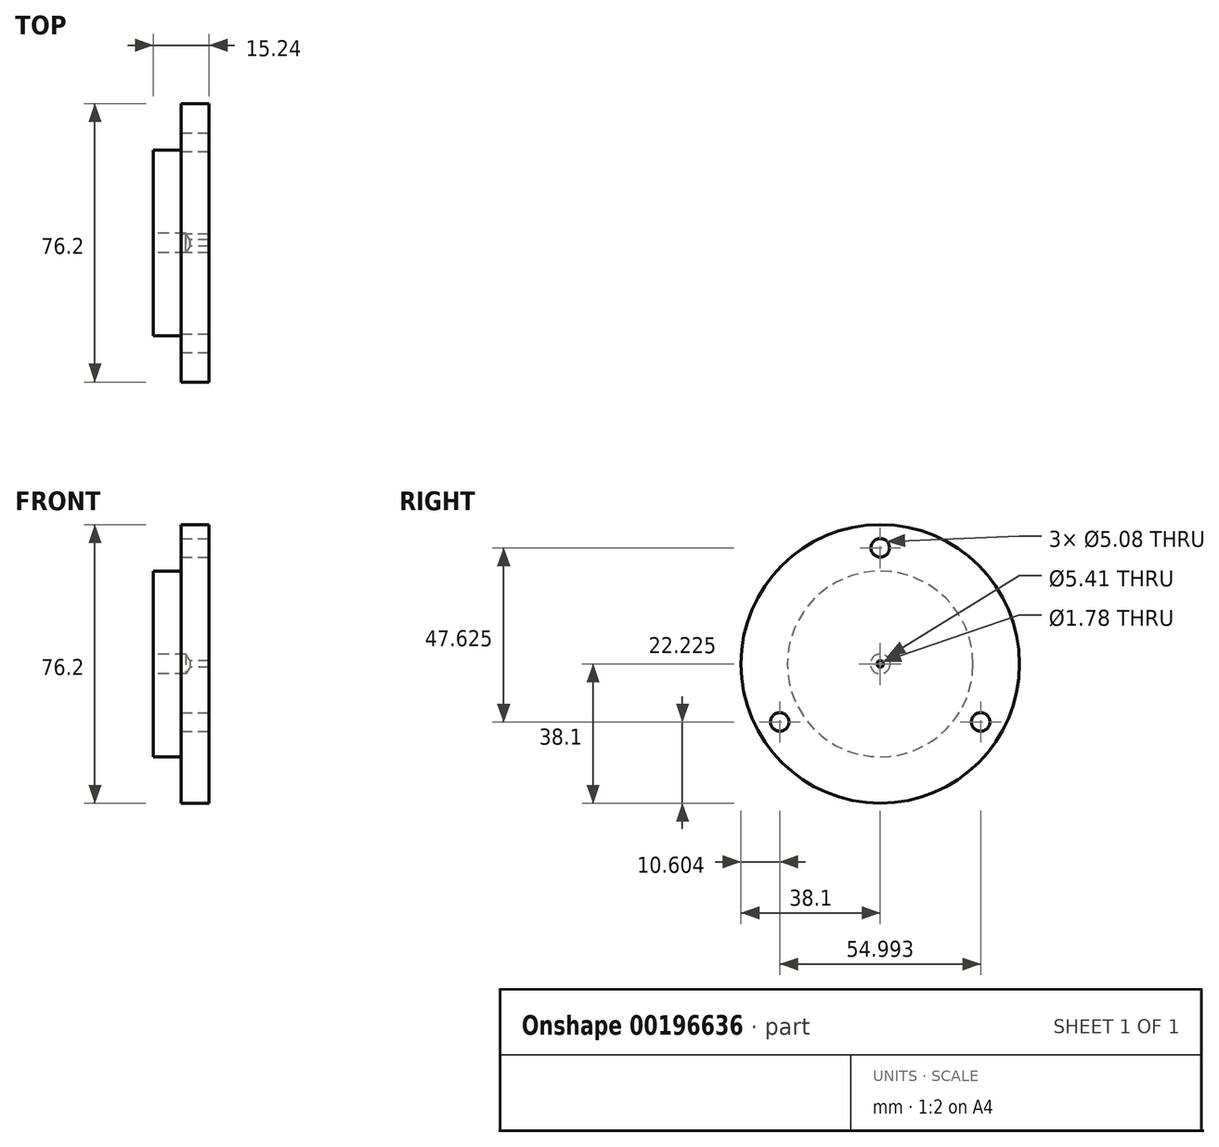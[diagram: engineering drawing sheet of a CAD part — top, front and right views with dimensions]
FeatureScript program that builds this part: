
annotation { "Feature Type Name" : "Feature", "Feature Type Description" : "" }
export const myFeature = defineFeature(function(context is Context, id is Id, definition is map)
    precondition{}
    {
        {
            var Q0;
            Q0=qCreatedBy(makeId("Right.planeOp"),FACE);
            var sketch = newSketch(context, id + "F0", { "sketchPlane" : qUnion([Q0])});
            skCircle(sketch, "E0", {"center": v(0, 0) * mm, "radius": 25.4 * mm});
            skSolve(sketch);
        }
        {
            var Q0;
            Q0=makeQuery(id+"F0.imprint","IMPRINT",FACE,{"disambiguationData":[TD([[makeQuery(id+"F0.imprint","IMPRINT",EDGE,{"derivedFrom":sQuery(id+"F0.wireOp",EDGE,"E0")}),1.0]])]});
            extrude(context, id + "F1", {"entities" : qUnion([Q0]), "depth" : 7.62 * mm});
        }
        {
            var Q0;
            Q0=makeQuery(id+"F1.opExtrude","CAP_FACE",FACE,{"disambiguationData":[OSD([sQuery(id+"F0.wireOp",EDGE,"E0")])],"isStart":false});
            var sketch = newSketch(context, id + "F2", { "sketchPlane" : qUnion([Q0])});
            skCircle(sketch, "E1", {"center": v(0, 0) * mm, "radius": 38.1 * mm});
            skSolve(sketch);
        }
        {
            var Q0;
            Q0 = qSketchRegion(id + "F2", true);
            var Q1;
            Q1=makeQuery(id+"F1.opExtrude","CAP_FACE",FACE,{"disambiguationData":[OSD([sQuery(id+"F0.wireOp",EDGE,"E0")])],"isStart":true});
            var Q2;
            Q2=sQuery(id+"F2.wireOp",EDGE,"E1");
            extrude(context, id + "F3", {"entities" : qUnion([Q0, Q1]), "operationType" : NewBodyOperationType.ADD, "surfaceEntities" : qUnion([Q2]), "depth" : 7.62 * mm});
        }
        {
            var Q0;
            Q0=makeQuery(id+"F3.opExtrude","CAP_FACE",FACE,{"disambiguationData":[OSD([sQuery(id+"F2.wireOp",EDGE,"E1")])],"isStart":false});
            var sketch = newSketch(context, id + "F4", { "sketchPlane" : qUnion([Q0])});
            skCircle(sketch, "E2", {"center": v(0, 31.75) * mm, "radius": 2.54 * mm});
            skCircle(sketch, "E3", {"center": v(27.5, -15.88) * mm, "radius": 2.54 * mm});
            skCircle(sketch, "E4", {"center": v(-27.5, -15.88) * mm, "radius": 2.54 * mm});
            skSolve(sketch);
        }
        {
            var Q0;
            Q0 = qSketchRegion(id + "F4", true);
            extrude(context, id + "F5", {"entities" : qUnion([Q0]), "operationType" : NewBodyOperationType.REMOVE, "oppositeDirection" : true, "depth" : 7.62 * mm});
        }
        {
            var Q0;
            Q0=makeQuery(id+"F1.opExtrude","CAP_FACE",FACE,{"disambiguationData":[OSD([sQuery(id+"F0.wireOp",EDGE,"E0")])],"isStart":true});
            var sketch = newSketch(context, id + "F6", { "sketchPlane" : qUnion([Q0])});
            skPoint(sketch, "E5", {"position": v(0, 0) * mm});
            skSolve(sketch);
        }
        {
            var Q0;
            Q0=sQuery(id+"F6.wireOp",VERTEX,"E5");
            var Q1;
            Q1=makeQuery(id+"F1.opExtrude","SWEPT_BODY",BODY,{"disambiguationData":[OSD([sQuery(id+"F0.wireOp",EDGE,"E0")])]});
            hole(context, id + "F7", {"style" : HoleStyle.SIMPLE, "endStyle" : HoleEndStyle.BLIND, "standardTappedOrClearance" : lookupTablePath({ "standard" : "ANSI", "engagement" : "75%", "pitch" : "28 tpi", "size" : "1/4", "type" : "Tapped" }), "standardBlindInLast" : lookupTablePath({ "standard" : "ANSI", "engagement" : "75%", "pitch" : "28 tpi", "size" : "1/4", "type" : "Tapped" }), "holeDiameter" : 5.4 * mm, "holeDepth" : 8.9 * mm, "locations" : qUnion([Q0]), "scope" : qUnion([Q1]), "majorDiameter" : 6.35 * mm});
        }
        {
            var Q0;
            Q0=sQuery(id+"F6.wireOp",VERTEX,"E5");
            var Q1;
            Q1=makeQuery(id+"F1.opExtrude","SWEPT_BODY",BODY,{"disambiguationData":[OSD([sQuery(id+"F0.wireOp",EDGE,"E0")])]});
            hole(context, id + "F8", {"style" : HoleStyle.SIMPLE, "endStyle" : HoleEndStyle.THROUGH, "holeDiameter" : 1.78 * mm, "locations" : qUnion([Q0]), "scope" : qUnion([Q1]), "isTappedThrough" : true});
        }
    });
